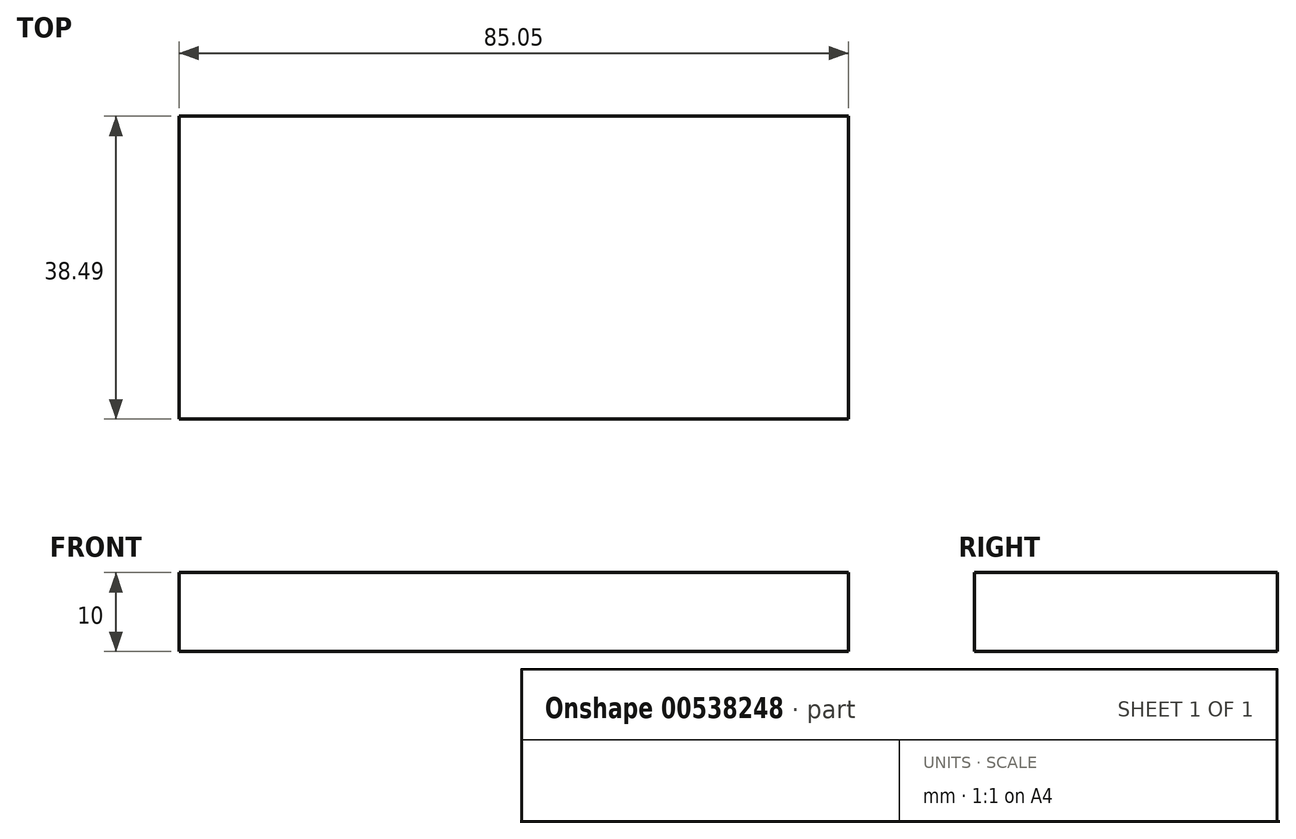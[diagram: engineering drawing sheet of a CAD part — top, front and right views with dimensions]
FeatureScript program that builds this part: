
annotation { "Feature Type Name" : "Feature", "Feature Type Description" : "" }
export const myFeature = defineFeature(function(context is Context, id is Id, definition is map)
    precondition{}
    {
        {
            var Q0;
            Q0=qCreatedBy(makeId("Top.planeOp"),FACE);
            var sketch = newSketch(context, id + "F0", { "sketchPlane" : qUnion([Q0])});
            skLineSegment(sketch, "E0.bottom", {"start": v(-40.77, 16.59) * mm, "end": v(44.28, 16.59) * mm});
            skLineSegment(sketch, "E0.top", {"start": v(-40.77, -21.9) * mm, "end": v(44.28, -21.9) * mm});
            skLineSegment(sketch, "E0.left", {"start": v(-40.77, 16.59) * mm, "end": v(-40.77, -21.9) * mm});
            skLineSegment(sketch, "E0.right", {"start": v(44.28, 16.59) * mm, "end": v(44.28, -21.9) * mm});
            skSolve(sketch);
        }
        {
            var Q0;
            Q0=makeQuery(id+"F0.imprint","IMPRINT",FACE,{"disambiguationData":[TD([[makeQuery(id+"F0.imprint","IMPRINT",EDGE,{"derivedFrom":sQuery(id+"F0.wireOp",EDGE,"E0.bottom")}),-1.0]])]});
            extrude(context, id + "F1", {"entities" : qUnion([Q0]), "depth" : 10 * mm, "offsetDistance" : 25 * mm});
        }
    });
